# Revit family: Haworth_BuzziMilk_Stool
name_source: partatom
category: Furniture
revit_build: Autodesk Revit 2018 (Build: 20170223_1515(x64)
units: mm (PartAtom-declared; Revit-internal decimal feet)

## family parameters
Always vertical = Yes
Cut with Voids When Loaded = No
OmniClass Number = 23.40.20.00
OmniClass Title = General Furniture and Specialties
Room Calculation Point = No
Shared = No
Work Plane-Based = No

## types (4) — shared parameters
Assembly Code = E2020200
Manufacturer = Haworth
Model = HCBZ-MKS
Note = Verify Final Dim. w/ Haworth
Revision = 1
URL = http://www.haworth.com
URL - Product = https://www.haworth.com
Warranty = http://www.haworth.com
zero-valued in all types: Actual Depth, Actual Height, Actual Width, Cushion Height

## per-type parameters (varying)
| type | Cushion | Cushion Control | Description | High | Low | Medium | Wood Top |
| HCBZ-MKS1 | Yes | Yes | Haworth BuzziMilk Stool - Low - Upholstered | No | Yes | No | No |
| HCBZ-MKS2 | Yes | Yes | Haworth BuzziMilk Stool - Medium - Upholstered | No | No | Yes | No |
| HCBZ-MKS3 | Yes | Yes | Haworth BuzziMilk Stool - High - Upholstered | Yes | No | No | No |
| HCBZ-MKS1-W | No | No | Haworth BuzziMilk Stool - Low - Wood | No | Yes | No | Yes |

## geometry (parser evidence)
native form markers: Sweep x2
no freeform markers — native parametric forms only
